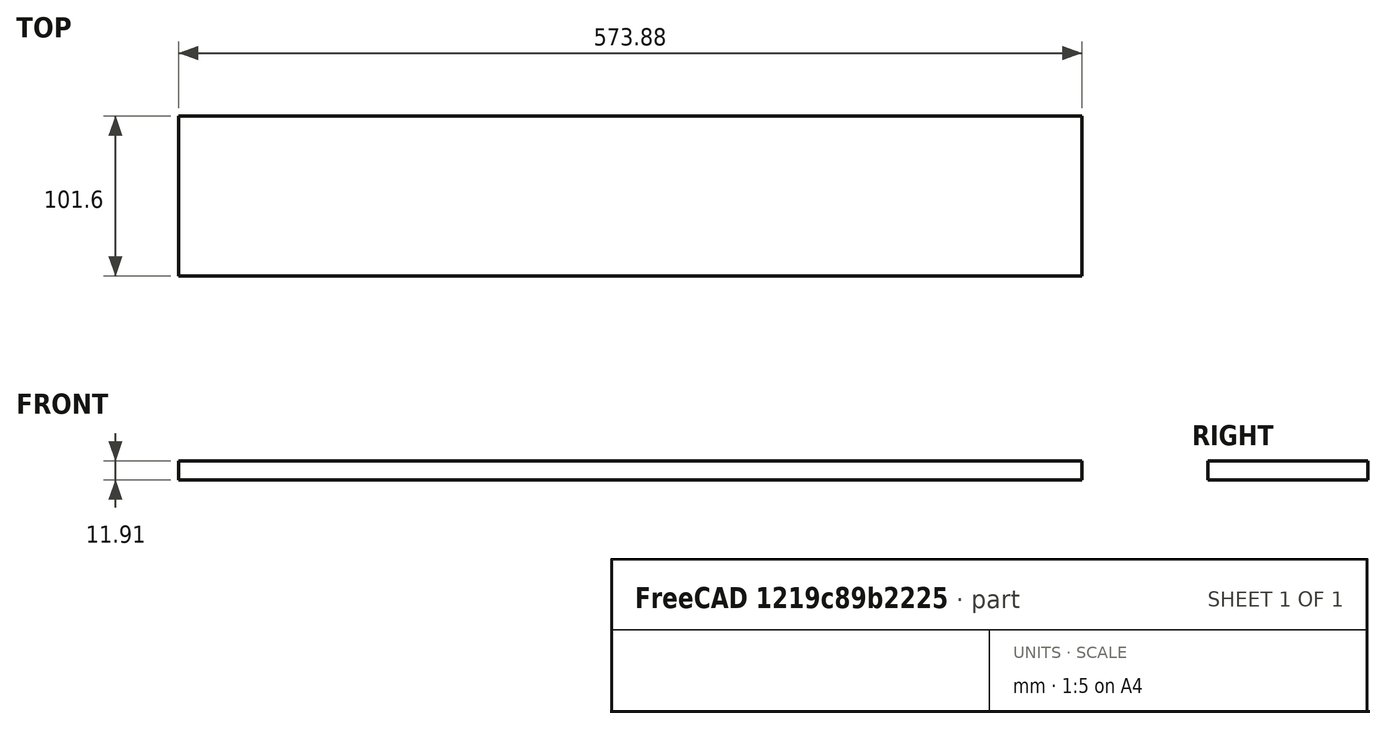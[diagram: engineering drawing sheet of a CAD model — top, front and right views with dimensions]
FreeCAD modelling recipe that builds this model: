
FCSTD DOCUMENT  (FreeCAD 0.20R29603 (Git))
Label: ShortSkirt
License: All rights reserved
LicenseURL: http://en.wikipedia.org/wiki/All_rights_reserved
objects: App::DocumentObjectGroup×3, Sketcher::SketchObject×1, PartDesign::Pad×1, PartDesign::Body×1, PartDesign::CoordinateSystem×1, App::FeaturePython×1, App::Part×1
note: 5 computed .brp shape members not serialized (recipe doc carries the construction recipe); baked Part::Feature solids carry a one-line shape summary decoded from their .brp
EXTERNAL_REF file=Parameters.FCStd obj=Spreadsheet

FEATURE [Sketcher::SketchObject] Sketch
  FullyConstrained = true
  MapMode = 5
  Support = -> [XY_Plane]
  expr: Constraints[8] = Parameters#<<DeskDimensions>>.Skirt_Width
  expr: Constraints[9] = Parameters#<<DeskDimensions>>.Skirt_Height
  sketch-geometry (4):
    g0: LineSegment StartX=-286.941 StartY=0 StartZ=0 EndX=286.941 EndY=0 EndZ=0
    g1: LineSegment StartX=286.941 StartY=0 StartZ=0 EndX=286.941 EndY=-101.6 EndZ=0
    g2: LineSegment StartX=286.941 StartY=-101.6 StartZ=0 EndX=-286.941 EndY=-101.6 EndZ=0
    g3: LineSegment StartX=-286.941 StartY=-101.6 StartZ=0 EndX=-286.941 EndY=0 EndZ=0
  constraints (11):
    c: Coincident(g0,g1)
    c: Coincident(g1,g2)
    c: Coincident(g2,g3)
    c: Coincident(g3,g0)
    c: Horizontal(g0)
    c: Horizontal(g2)
    c: Vertical(g1)
    c: Vertical(g3)
    c: DistanceX(g0,g0) = 573.881
    c: DistanceY(g3,g3) = 101.6
    c: Symmetric(g0,g0,g-1)
FEATURE [PartDesign::Pad] Pad
  Direction = (0,0,1)
  Length = 11.9062
  Length2 = 10
  Profile = -> Sketch
  ReferenceAxis = -> Sketch [N_Axis]
  Type = 0
  expr: Length = Parameters#<<DeskDimensions>>.Stock_Thickness
FEATURE [PartDesign::Body] Body
  Group = -> [Sketch,Pad]
  Origin = -> Origin
  Tip = -> Pad
FEATURE [App::DocumentObjectGroup] Parts
FEATURE [PartDesign::CoordinateSystem] LCS_Origin
  AttacherType = Attacher::AttachEngine3D
  MapMode = 2
  Support = -> [X_Axis001]
FEATURE [App::DocumentObjectGroup] Constraints
FEATURE [App::FeaturePython] Variables  # WARN: FeaturePython — macro-defined, semantics opaque (R4)
  Type = App::PropertyContainer
FEATURE [App::DocumentObjectGroup] Configurations
FEATURE [App::Part] Model
  Group = -> [LCS_Origin,Constraints,Variables,Configurations,Body]
  Origin = -> Origin001
  Type = Assembly
